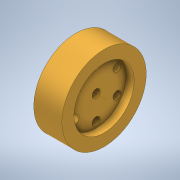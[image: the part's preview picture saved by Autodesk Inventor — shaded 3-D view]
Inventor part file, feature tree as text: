
AUTODESK INVENTOR PART (.ipt)
format: ipt  version: 2021.1 (Build 251245000, 245)  size: 164,352 bytes
history: native  units: in
note: dims shown in document units (in); Inventor stores cm internally (conversion verified against a paired STEP export)
features: projected_geometry x5, sketch x4, extrude x3, revolve x1
ambient origin geometry x8: Origin, YZ Plane, XZ Plane, XY Plane, X Axis, Y Axis, Z Axis, Center Point
bodies: Solid1 (feature_tree)
feature tree (13):
  extrude  "Extrusion1"  Depth=1.4in TaperAngle=0.0deg
  extrude  "Extrusion2"  Depth=0.4in TaperAngle=0.0deg
  extrude  "Extrusion3"  Depth=0.4in
  revolve  "Revolution1"  [1 undecoded]
  sketch  "Sketch1"  dims[d0=4.2in d1=1.4in d2=0.0in]
  sketch  "Sketch2"  dims[d3=3.0in d4=0.4in d5=0.0in]
  sketch  "Sketch3"  dims[d6=2.4in d7=0.4in]
  sketch  "Sketch4"  dims[d8=2.3622in d10=360.0deg d12=0.0in d13=0.0in d14=0.4in d15=1.0in d16=0.4in d17=0.2in d18=0.3in d19=90.0deg]
  projected_geometry  "Projected Loop1"
  projected_geometry  "Projected Loop2"
  projected_geometry  "Project Cut Edges1"
  projected_geometry  "Project Cut Edges2"
  projected_geometry  "Project Cut Edges3"
note: 1 required parameter value undecoded (feature->parameter linkage not recoverable at this tier; creation-order binding heuristic only, values carry confidence <= 0.55)
